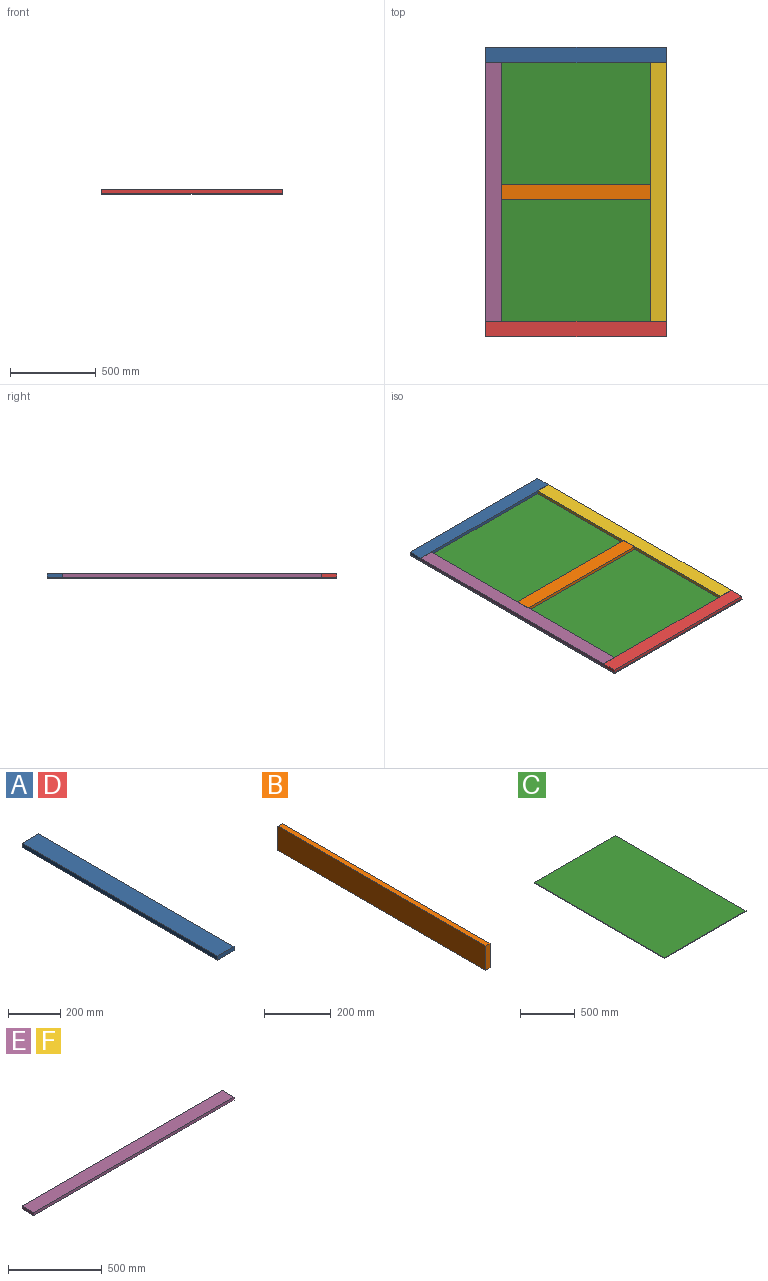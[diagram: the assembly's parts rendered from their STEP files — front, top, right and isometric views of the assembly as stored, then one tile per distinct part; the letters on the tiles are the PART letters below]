
ASSEMBLY  parts=6 mates=5
PART A: 6 faces, bbox 88.9x1054.1x19.1 mm
  f0: plane 1054.1x19.05mm, normal (-1,0,0), area 20080.6mm2, adj f1,f3,f4,f5
  f1: plane 1054.1x88.9mm, normal (0,0,-1), area 93709.5mm2, adj f0,f2,f4,f5
  f2: plane 1054.1x19.05mm, normal (1,0,0), area 20080.6mm2, adj f1,f3,f4,f5
  f3: plane 1054.1x88.9mm, normal (0,0,1), area 93709.5mm2, adj f0,f2,f4,f5
  f4: plane 88.9x19.05mm, normal (0,1,0), area 1693.5mm2, adj f0,f1,f2,f3
  f5: plane 88.9x19.05mm, normal (0,-1,0), area 1693.5mm2, adj f0,f1,f2,f3
PART B: 6 faces, bbox 19.1x876.3x88.9 mm
  f0: plane 876.3x19.05mm, normal (0,0,1), area 16693.5mm2, adj f1,f3,f4,f5
  f1: plane 876.3x88.9mm, normal (-1,0,0), area 77903.1mm2, adj f0,f2,f4,f5
  f2: plane 876.3x19.05mm, normal (0,0,-1), area 16693.5mm2, adj f1,f3,f4,f5
  f3: plane 876.3x88.9mm, normal (1,0,0), area 77903.1mm2, adj f0,f2,f4,f5
  f4: plane 88.9x19.05mm, normal (0,1,0), area 1693.5mm2, adj f0,f1,f2,f3
  f5: plane 88.9x19.05mm, normal (0,-1,0), area 1693.5mm2, adj f0,f1,f2,f3
PART C: 6 faces, bbox 1054.1x1689.1x6.4 mm
  f0: plane 1689.1x6.35mm, normal (-1,0,0), area 10725.8mm2, adj f1,f3,f4,f5
  f1: plane 1054.1x6.35mm, normal (0,-1,0), area 6693.5mm2, adj f0,f2,f4,f5
  f2: plane 1689.1x6.35mm, normal (1,0,0), area 10725.8mm2, adj f1,f3,f4,f5
  f3: plane 1054.1x6.35mm, normal (0,1,0), area 6693.5mm2, adj f0,f2,f4,f5
  f4: plane 1689.1x1054.1mm, normal (0,0,1), area 1780480.3mm2, adj f0,f1,f2,f3
  f5: plane 1689.1x1054.1mm, normal (0,0,-1), area 1780480.3mm2, adj f0,f1,f2,f3
PART D: same geometry as A
PART E: 6 faces, bbox 1511.3x88.9x19.1 mm
  f0: plane 1511.3x88.9mm, normal (0,0,1), area 134354.6mm2, adj f1,f3,f4,f5
  f1: plane 1511.3x19.05mm, normal (0,-1,0), area 28790.3mm2, adj f0,f2,f4,f5
  f2: plane 1511.3x88.9mm, normal (0,0,-1), area 134354.6mm2, adj f1,f3,f4,f5
  f3: plane 1511.3x19.05mm, normal (0,1,0), area 28790.3mm2, adj f0,f2,f4,f5
  f4: plane 88.9x19.05mm, normal (1,0,0), area 1693.5mm2, adj f0,f1,f2,f3
  f5: plane 88.9x19.05mm, normal (-1,0,0), area 1693.5mm2, adj f0,f1,f2,f3
PART F: same geometry as E
PLACE A rot(axis=(0,0,-1),90deg) t=(153.93,1296.59,135.84)mm
PLACE B rot(axis=(-0.58,-0.58,-0.58),120deg) t=(242.83,455.5,135.84)mm
PLACE C t=(181.83,-314.95,129.49)mm
PLACE D rot(axis=(0,0,-1),90deg) t=(153.93,-303.61,135.84)mm
PLACE E rot(axis=(0,0,-1),90deg) t=(186.55,1237.26,148.04)mm
PLACE F rot(axis=(0,0,-1),90deg) t=(1151.75,1237.26,148.04)mm
MATE fastened D.f1 <-> C.f4  axis (0,0,-1) through (680.98,-362.94,135.84)mm
MATE fastened B.f1 <-> C.f4  axis (0,0,-1) through (680.98,481.61,135.84)mm
MATE fastened F.f2 <-> C.f4  axis (0,0,-1) through (1208.03,481.61,135.84)mm
MATE fastened E.f2 <-> C.f4  axis (0,0,-1) through (153.93,481.61,135.84)mm
MATE fastened A.f1 <-> C.f4  axis (0,0,-1) through (680.98,1326.16,135.84)mm
